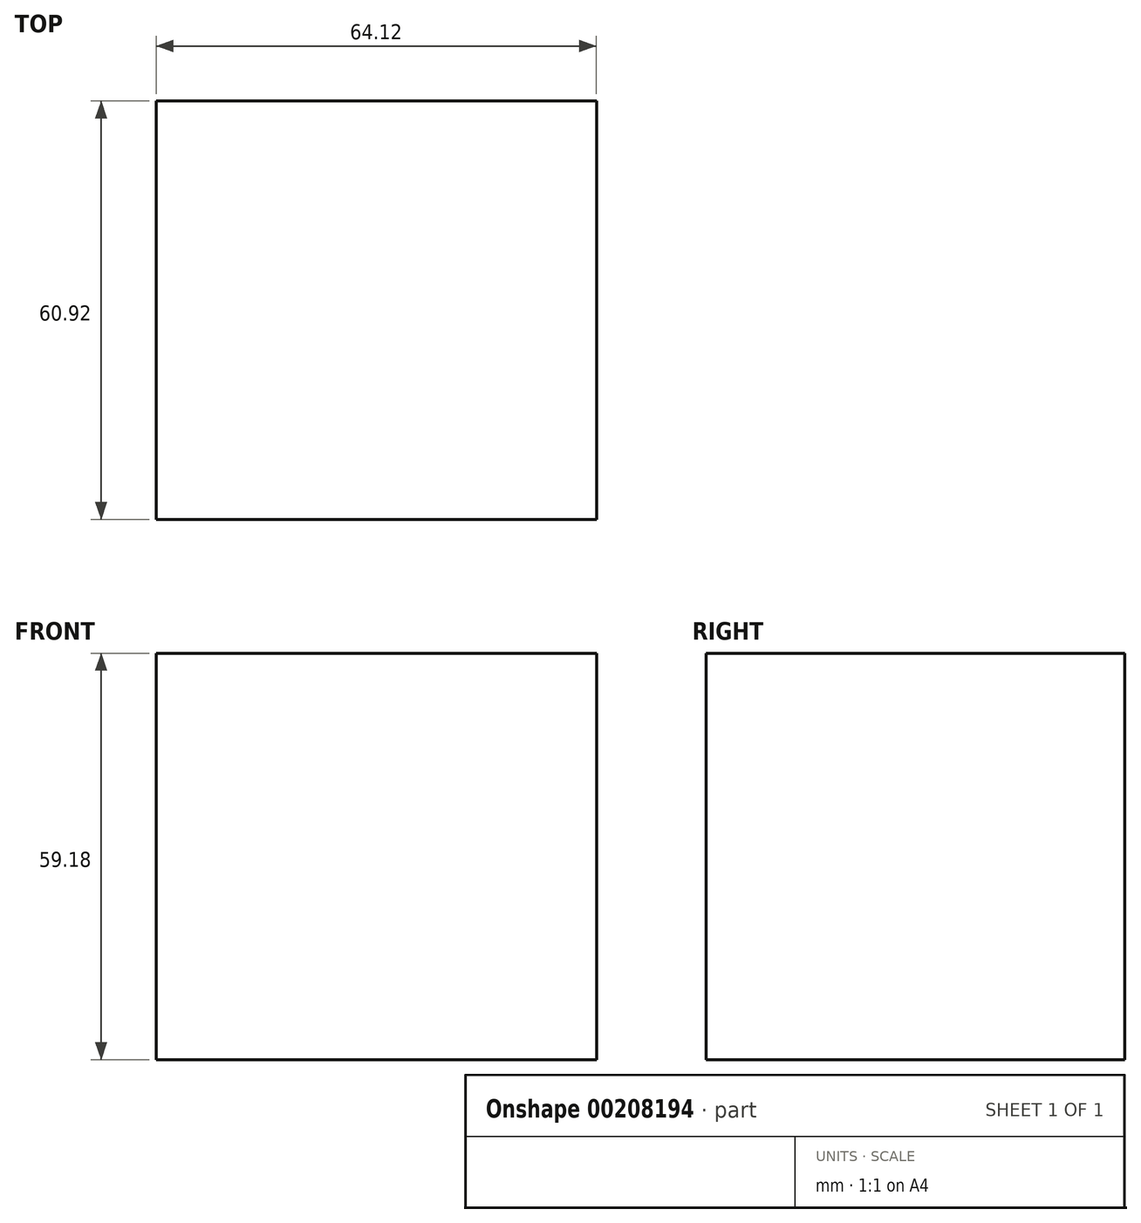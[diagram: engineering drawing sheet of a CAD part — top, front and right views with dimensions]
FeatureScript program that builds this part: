
annotation { "Feature Type Name" : "Feature", "Feature Type Description" : "" }
export const myFeature = defineFeature(function(context is Context, id is Id, definition is map)
    precondition{}
    {
        {
            var Q0;
            Q0=qCreatedBy(makeId("Top.planeOp"),FACE);
            var sketch = newSketch(context, id + "F0", { "sketchPlane" : qUnion([Q0])});
            skLineSegment(sketch, "E0.bottom", {"start": v(-32.06, 30.46) * mm, "end": v(32.06, 30.46) * mm});
            skLineSegment(sketch, "E0.top", {"start": v(-32.06, -30.46) * mm, "end": v(32.06, -30.46) * mm});
            skLineSegment(sketch, "E0.left", {"start": v(-32.06, 30.46) * mm, "end": v(-32.06, -30.46) * mm});
            skLineSegment(sketch, "E0.right", {"start": v(32.06, 30.46) * mm, "end": v(32.06, -30.46) * mm});
            skPoint(sketch, "E0.middle", {"position": v(0, 0) * mm});
            skSolve(sketch);
        }
        {
            var Q0;
            Q0 = qSketchRegion(id + "F0", true);
            extrude(context, id + "F1", {"entities" : qUnion([Q0]), "depth" : 59.18 * mm});
        }
    });
